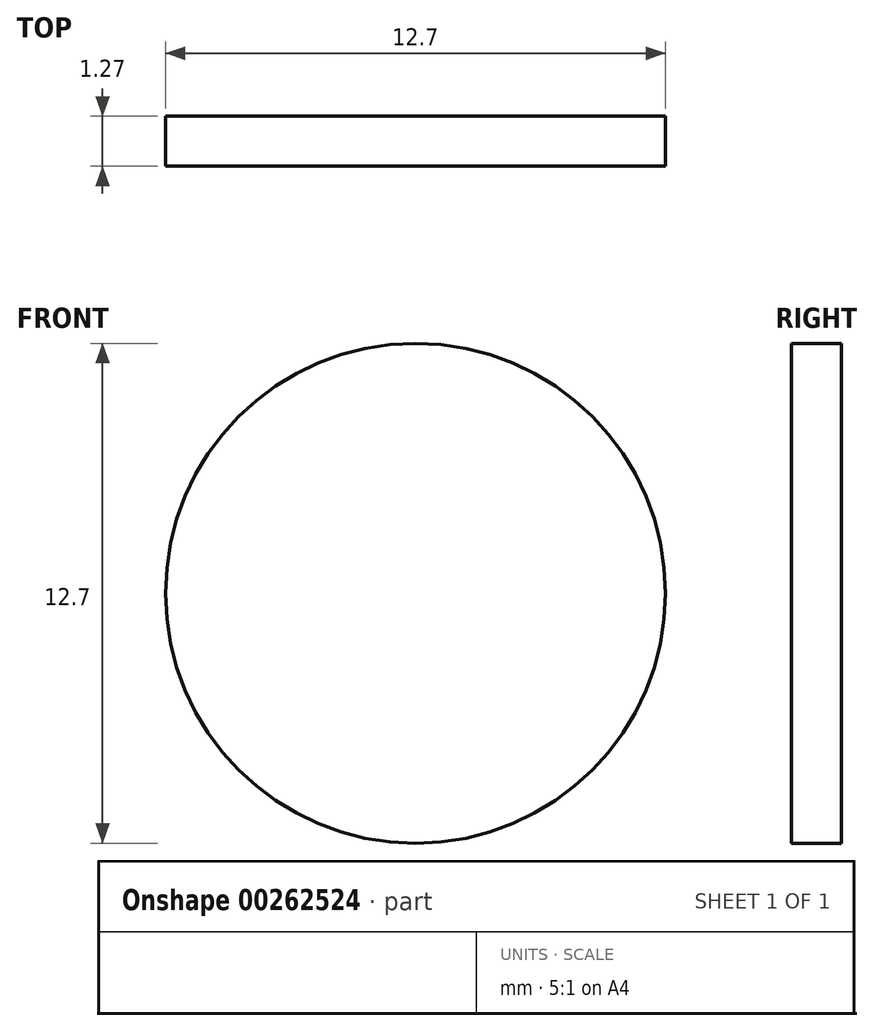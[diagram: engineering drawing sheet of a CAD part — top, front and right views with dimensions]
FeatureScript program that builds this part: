
annotation { "Feature Type Name" : "Feature", "Feature Type Description" : "" }
export const myFeature = defineFeature(function(context is Context, id is Id, definition is map)
    precondition{}
    {
        {
            var Q0;
            Q0=qCreatedBy(makeId("Front.planeOp"),FACE);
            var sketch = newSketch(context, id + "F0", { "sketchPlane" : qUnion([Q0])});
            skCircle(sketch, "E0", {"center": v(0, 0) * mm, "radius": 6.35 * mm});
            skSolve(sketch);
        }
        {
            var Q0;
            Q0 = qSketchRegion(id + "F0", true);
            extrude(context, id + "F1", {"entities" : qUnion([Q0]), "oppositeDirection" : true, "depth" : 1.27 * mm});
        }
    });
